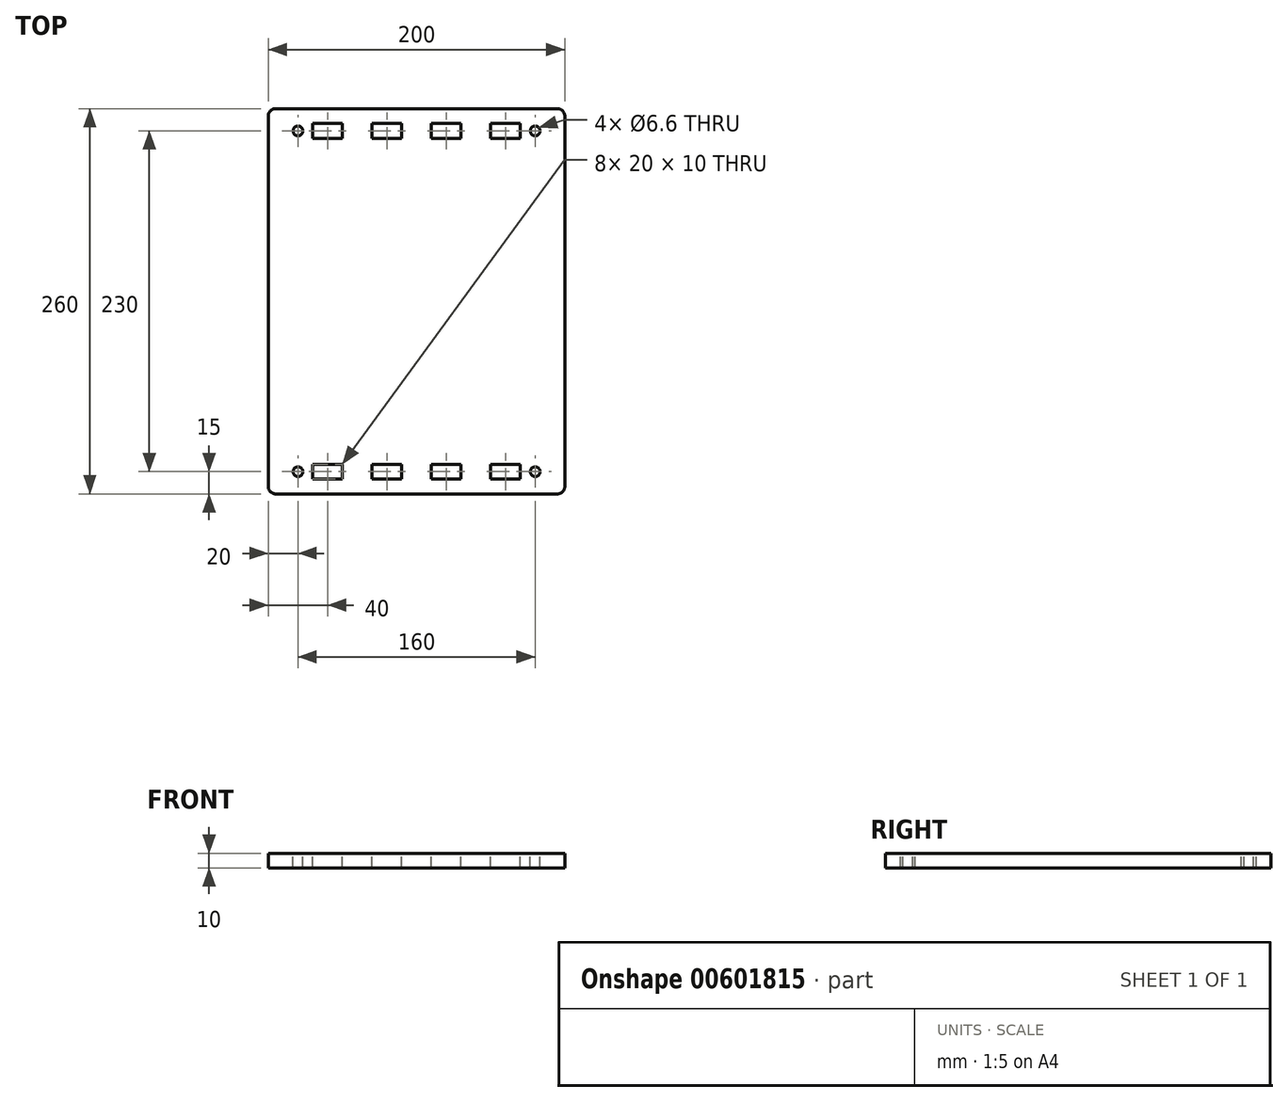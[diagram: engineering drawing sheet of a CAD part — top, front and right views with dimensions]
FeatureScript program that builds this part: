
annotation { "Feature Type Name" : "Feature", "Feature Type Description" : "" }
export const myFeature = defineFeature(function(context is Context, id is Id, definition is map)
    precondition{}
    {
        {
            var Q0;
            Q0=qCreatedBy(makeId("Top.planeOp"),FACE);
            var sketch = newSketch(context, id + "F0", { "sketchPlane" : qUnion([Q0])});
            skLineSegment(sketch, "E0.bottom", {"start": v(95, 130) * mm, "end": v(-95, 130) * mm});
            skLineSegment(sketch, "E0.top", {"start": v(95, -130) * mm, "end": v(-95, -130) * mm});
            skLineSegment(sketch, "E0.left", {"start": v(100, 125) * mm, "end": v(100, -125) * mm});
            skLineSegment(sketch, "E0.right", {"start": v(-100, 125) * mm, "end": v(-100, -125) * mm});
            skPoint(sketch, "E0.middle", {"position": v(0, 0) * mm});
            skPoint(sketch, "E1.visualSharp", {"position": v(-100, 130) * mm});
            skArc(sketch, "E1.filletArc", {"start": v(-95, 130) * mm, "mid": v(-98.54, 128.54) * mm, "end": v(-100, 125) * mm});
            skPoint(sketch, "E2.visualSharp", {"position": v(100, 130) * mm});
            skArc(sketch, "E2.filletArc", {"start": v(100, 125) * mm, "mid": v(98.54, 128.54) * mm, "end": v(95, 130) * mm});
            skPoint(sketch, "E3.visualSharp", {"position": v(100, -130) * mm});
            skArc(sketch, "E3.filletArc", {"start": v(95, -130) * mm, "mid": v(98.54, -128.54) * mm, "end": v(100, -125) * mm});
            skPoint(sketch, "E4.visualSharp", {"position": v(-100, -130) * mm});
            skArc(sketch, "E4.filletArc", {"start": v(-100, -125) * mm, "mid": v(-98.54, -128.54) * mm, "end": v(-95, -130) * mm});
            skSolve(sketch);
        }
        {
            var Q0;
            Q0 = qSketchRegion(id + "F0", true);
            extrude(context, id + "F1", {"entities" : qUnion([Q0]), "depth" : 10 * mm, "offsetDistance" : 25 * mm});
        }
        {
            var Q0;
            Q0=makeQuery(id+"F1.opExtrude","CAP_FACE",FACE,{"disambiguationData":[OSD([sQuery(id+"F0.wireOp",EDGE,"E0.bottom"),sQuery(id+"F0.wireOp",EDGE,"E0.top"),sQuery(id+"F0.wireOp",EDGE,"E0.left"),sQuery(id+"F0.wireOp",EDGE,"E0.right"),sQuery(id+"F0.wireOp",EDGE,"E1.filletArc"),sQuery(id+"F0.wireOp",EDGE,"E2.filletArc"),sQuery(id+"F0.wireOp",EDGE,"E3.filletArc"),sQuery(id+"F0.wireOp",EDGE,"E4.filletArc")])],"isStart":false});
            var sketch = newSketch(context, id + "F2", { "sketchPlane" : qUnion([Q0])});
            skLineSegment(sketch, "E5.bottom", {"start": v(-70, -120) * mm, "end": v(-50, -120) * mm});
            skLineSegment(sketch, "E5.top", {"start": v(-70, -110) * mm, "end": v(-50, -110) * mm});
            skLineSegment(sketch, "E5.left", {"start": v(-70, -120) * mm, "end": v(-70, -110) * mm});
            skLineSegment(sketch, "E5.right", {"start": v(-50, -120) * mm, "end": v(-50, -110) * mm});
            skLineSegment(sketch, "E6.bottom", {"start": v(-30, -120) * mm, "end": v(-10, -120) * mm});
            skLineSegment(sketch, "E6.top", {"start": v(-30, -110) * mm, "end": v(-10, -110) * mm});
            skLineSegment(sketch, "E6.left", {"start": v(-30, -120) * mm, "end": v(-30, -110) * mm});
            skLineSegment(sketch, "E6.right", {"start": v(-10, -120) * mm, "end": v(-10, -110) * mm});
            skLineSegment(sketch, "E7.MirrorCS", {"start": v(30, -120) * mm, "end": v(10, -120) * mm});
            skLineSegment(sketch, "E8.MirrorCS", {"start": v(10, -120) * mm, "end": v(10, -110) * mm});
            skLineSegment(sketch, "E9.MirrorCS", {"start": v(30, -110) * mm, "end": v(10, -110) * mm});
            skLineSegment(sketch, "E10.MirrorCS", {"start": v(30, -120) * mm, "end": v(30, -110) * mm});
            skLineSegment(sketch, "E11.MirrorCS", {"start": v(70, -120) * mm, "end": v(50, -120) * mm});
            skLineSegment(sketch, "E12.MirrorCS", {"start": v(50, -120) * mm, "end": v(50, -110) * mm});
            skLineSegment(sketch, "E13.MirrorCS", {"start": v(70, -110) * mm, "end": v(50, -110) * mm});
            skLineSegment(sketch, "E14.MirrorCS", {"start": v(70, -120) * mm, "end": v(70, -110) * mm});
            skLineSegment(sketch, "E15.MirrorCS", {"start": v(70, 120) * mm, "end": v(70, 110) * mm});
            skLineSegment(sketch, "E16.MirrorCS", {"start": v(-70, 120) * mm, "end": v(-70, 110) * mm});
            skLineSegment(sketch, "E17.MirrorCS", {"start": v(50, 120) * mm, "end": v(50, 110) * mm});
            skLineSegment(sketch, "E18.MirrorCS", {"start": v(-50, 120) * mm, "end": v(-50, 110) * mm});
            skLineSegment(sketch, "E19.MirrorCS", {"start": v(30, 120) * mm, "end": v(30, 110) * mm});
            skLineSegment(sketch, "E20.MirrorCS", {"start": v(10, 120) * mm, "end": v(10, 110) * mm});
            skLineSegment(sketch, "E21.MirrorCS", {"start": v(-30, 120) * mm, "end": v(-30, 110) * mm});
            skLineSegment(sketch, "E22.MirrorCS", {"start": v(-10, 120) * mm, "end": v(-10, 110) * mm});
            skLineSegment(sketch, "E23.MirrorCS", {"start": v(-70, 120) * mm, "end": v(-50, 120) * mm});
            skLineSegment(sketch, "E24.MirrorCS", {"start": v(-70, 110) * mm, "end": v(-50, 110) * mm});
            skLineSegment(sketch, "E25.MirrorCS", {"start": v(70, 110) * mm, "end": v(50, 110) * mm});
            skLineSegment(sketch, "E26.MirrorCS", {"start": v(-30, 120) * mm, "end": v(-10, 120) * mm});
            skLineSegment(sketch, "E27.MirrorCS", {"start": v(70, 120) * mm, "end": v(50, 120) * mm});
            skLineSegment(sketch, "E28.MirrorCS", {"start": v(30, 110) * mm, "end": v(10, 110) * mm});
            skLineSegment(sketch, "E29.MirrorCS", {"start": v(-30, 110) * mm, "end": v(-10, 110) * mm});
            skLineSegment(sketch, "E30.MirrorCS", {"start": v(30, 120) * mm, "end": v(10, 120) * mm});
            skSolve(sketch);
        }
        {
            var Q0;
            Q0 = qSketchRegion(id + "F2", true);
            extrude(context, id + "F3", {"entities" : qUnion([Q0]), "operationType" : NewBodyOperationType.REMOVE, "endBound" : BoundingType.UP_TO_NEXT, "oppositeDirection" : true, "depth" : 25 * mm, "offsetDistance" : 25 * mm});
        }
        {
            var Q0;
            Q0=makeQuery(id+"F1.opExtrude","CAP_FACE",FACE,{"disambiguationData":[OSD([sQuery(id+"F0.wireOp",EDGE,"E0.bottom"),sQuery(id+"F0.wireOp",EDGE,"E0.top"),sQuery(id+"F0.wireOp",EDGE,"E0.left"),sQuery(id+"F0.wireOp",EDGE,"E0.right"),sQuery(id+"F0.wireOp",EDGE,"E1.filletArc"),sQuery(id+"F0.wireOp",EDGE,"E2.filletArc"),sQuery(id+"F0.wireOp",EDGE,"E3.filletArc"),sQuery(id+"F0.wireOp",EDGE,"E4.filletArc")])],"isStart":false});
            var sketch = newSketch(context, id + "F4", { "sketchPlane" : qUnion([Q0])});
            skLineSegment(sketch, "E31.bottom", {"start": v(80, 115) * mm, "end": v(-80, 115) * mm, "construction": true});
            skLineSegment(sketch, "E31.top", {"start": v(80, -115) * mm, "end": v(-80, -115) * mm, "construction": true});
            skLineSegment(sketch, "E31.left", {"start": v(80, 115) * mm, "end": v(80, -115) * mm, "construction": true});
            skLineSegment(sketch, "E31.right", {"start": v(-80, 115) * mm, "end": v(-80, -115) * mm, "construction": true});
            skPoint(sketch, "E31.middle", {"position": v(0, 0) * mm});
            skSolve(sketch);
        }
        {
            var Q0;
            Q0=sQuery(id+"F4.wireOp",VERTEX,"E31.right.start");
            var Q1;
            Q1=sQuery(id+"F4.wireOp",VERTEX,"E31.left.start");
            var Q2;
            Q2=sQuery(id+"F4.wireOp",VERTEX,"E31.left.end");
            var Q3;
            Q3=sQuery(id+"F4.wireOp",VERTEX,"E31.right.end");
            var Q4;
            Q4=makeQuery(id+"F1.opExtrude","SWEPT_BODY",BODY,{"disambiguationData":[OSD([sQuery(id+"F0.wireOp",EDGE,"E0.bottom"),sQuery(id+"F0.wireOp",EDGE,"E0.top"),sQuery(id+"F0.wireOp",EDGE,"E0.left"),sQuery(id+"F0.wireOp",EDGE,"E0.right"),sQuery(id+"F0.wireOp",EDGE,"E1.filletArc"),sQuery(id+"F0.wireOp",EDGE,"E2.filletArc"),sQuery(id+"F0.wireOp",EDGE,"E3.filletArc"),sQuery(id+"F0.wireOp",EDGE,"E4.filletArc")])]});
            hole(context, id + "F5", {"style" : HoleStyle.SIMPLE, "endStyle" : HoleEndStyle.THROUGH, "standardTappedOrClearance" : lookupTablePath({ "standard" : "ISO", "fit" : "Normal", "size" : "M6", "type" : "Clearance" }), "standardBlindInLast" : lookupTablePath({ "fit" : "Standard", "standard" : "ISO", "size" : "M6", "type" : "Clearance" }), "holeDiameter" : 6.6 * mm, "majorDiameter" : 5 * mm, "isTappedThrough" : true, "tappedDepth" : 12 * mm, "tapClearance" : 3, "locations" : qUnion([Q0, Q1, Q2, Q3]), "scope" : qUnion([Q4])});
        }
    });
